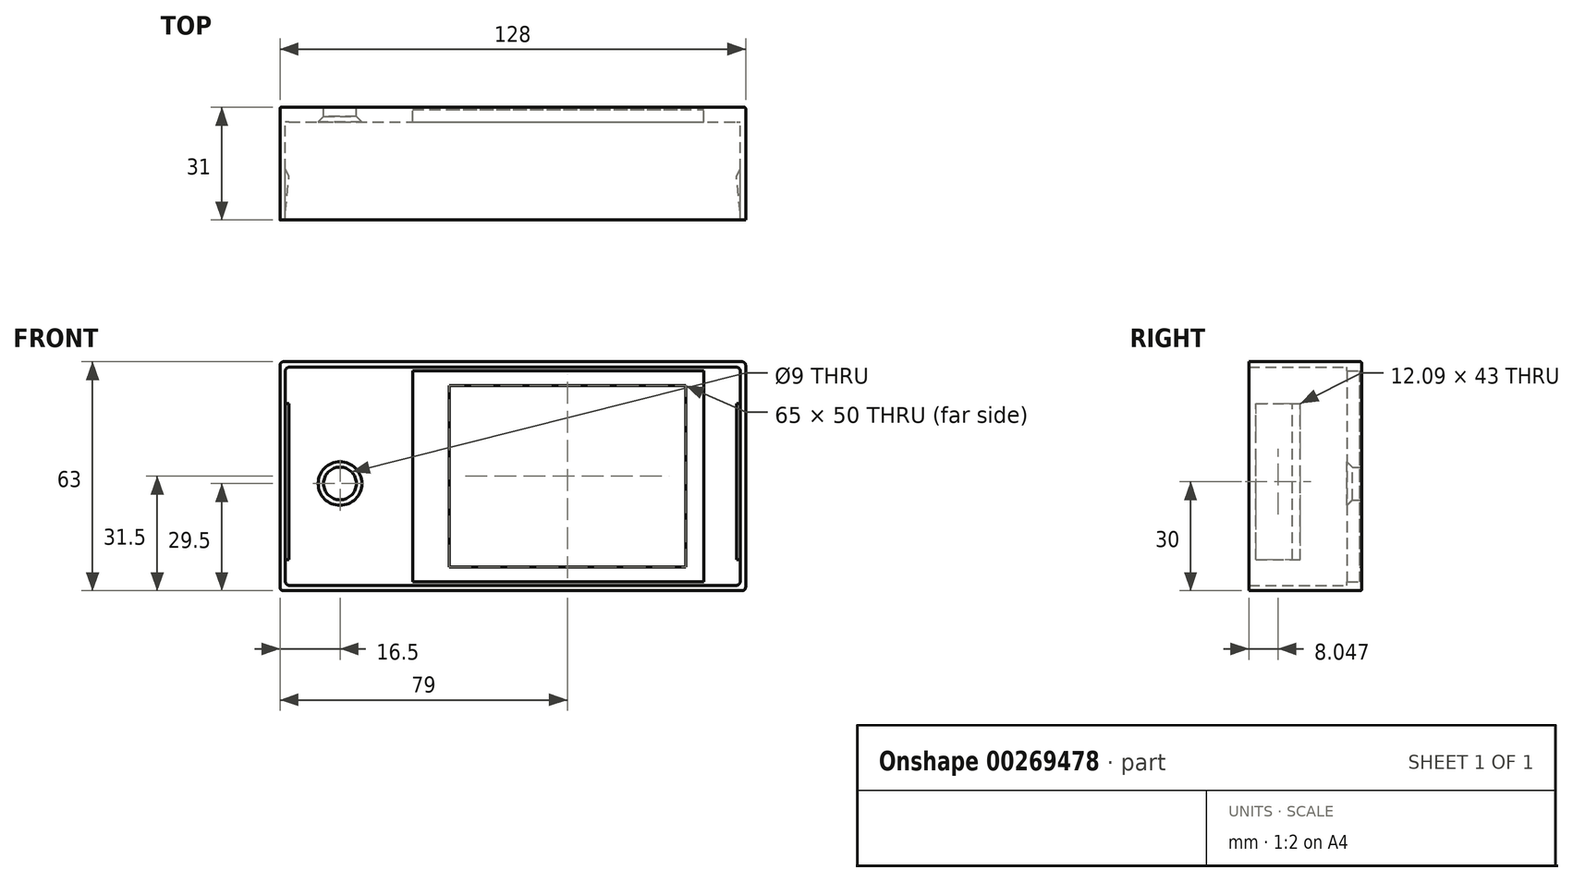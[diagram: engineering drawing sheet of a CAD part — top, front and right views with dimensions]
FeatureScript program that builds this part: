
annotation { "Feature Type Name" : "Feature", "Feature Type Description" : "" }
export const myFeature = defineFeature(function(context is Context, id is Id, definition is map)
    precondition{}
    {
        {
            var Q0;
            Q0=qCreatedBy(makeId("Front.planeOp"),FACE);
            var sketch = newSketch(context, id + "F0", { "sketchPlane" : qUnion([Q0])});
            skLineSegment(sketch, "E0.bottom", {"start": v(-64, 31.5) * mm, "end": v(64, 31.5) * mm});
            skLineSegment(sketch, "E0.top", {"start": v(-64, -31.5) * mm, "end": v(64, -31.5) * mm});
            skLineSegment(sketch, "E0.left", {"start": v(-64, 31.5) * mm, "end": v(-64, -31.5) * mm});
            skLineSegment(sketch, "E0.right", {"start": v(64, 31.5) * mm, "end": v(64, -31.5) * mm});
            skPoint(sketch, "E0.middle", {"position": v(0, 0) * mm});
            skLineSegment(sketch, "E1.0", {"start": v(-62.5, 30) * mm, "end": v(62.5, 30) * mm});
            skLineSegment(sketch, "E1.1", {"start": v(-62.5, 30) * mm, "end": v(-62.5, -30) * mm});
            skLineSegment(sketch, "E1.2", {"start": v(-62.5, -30) * mm, "end": v(62.5, -30) * mm});
            skLineSegment(sketch, "E1.3", {"start": v(62.5, 30) * mm, "end": v(62.5, -30) * mm});
            skLineSegment(sketch, "E2.bottom", {"start": v(-27.5, 29) * mm, "end": v(52.5, 29) * mm});
            skLineSegment(sketch, "E2.top", {"start": v(-27.5, -29) * mm, "end": v(52.5, -29) * mm});
            skLineSegment(sketch, "E2.left", {"start": v(-27.5, 29) * mm, "end": v(-27.5, -29) * mm});
            skLineSegment(sketch, "E2.right", {"start": v(52.5, 29) * mm, "end": v(52.5, -29) * mm});
            skLineSegment(sketch, "E3.bottom", {"start": v(-17.5, 25) * mm, "end": v(47.5, 25) * mm});
            skLineSegment(sketch, "E3.top", {"start": v(-17.5, -25) * mm, "end": v(47.5, -25) * mm});
            skLineSegment(sketch, "E3.left", {"start": v(-17.5, 25) * mm, "end": v(-17.5, -25) * mm});
            skLineSegment(sketch, "E3.right", {"start": v(47.5, 25) * mm, "end": v(47.5, -25) * mm});
            skCircle(sketch, "E4", {"center": v(-47.5, -2) * mm, "radius": 4.5 * mm});
            skSolve(sketch);
        }
        {
            var Q0;
            Q0=makeQuery(id+"F0.imprint","IMPRINT",FACE,{"disambiguationData":[TD([[makeQuery(id+"F0.imprint","IMPRINT",EDGE,{"derivedFrom":sQuery(id+"F0.wireOp",EDGE,"E0.bottom")}),-1.0]])]});
            extrude(context, id + "F1", {"entities" : qUnion([Q0]), "depth" : 31 * mm});
        }
        {
            var Q0;
            Q0=makeQuery(id+"F0.imprint","IMPRINT",FACE,{"disambiguationData":[TD([[makeQuery(id+"F0.imprint","IMPRINT",EDGE,{"derivedFrom":sQuery(id+"F0.wireOp",EDGE,"E2.bottom")}),-1.0]])]});
            var Q1;
            Q1=makeQuery(id+"F0.imprint","IMPRINT",FACE,{"disambiguationData":[TD([[makeQuery(id+"F0.imprint","IMPRINT",EDGE,{"derivedFrom":sQuery(id+"F0.wireOp",EDGE,"E1.0")}),-1.0]])]});
            extrude(context, id + "F2", {"entities" : qUnion([Q0, Q1]), "operationType" : NewBodyOperationType.ADD, "depth" : 4 * mm});
        }
        {
            var Q0;
            Q0=makeQuery(id+"F0.imprint","IMPRINT",FACE,{"disambiguationData":[TD([[makeQuery(id+"F0.imprint","IMPRINT",EDGE,{"derivedFrom":sQuery(id+"F0.wireOp",EDGE,"E2.bottom")}),-1.0]])]});
            extrude(context, id + "F3", {"entities" : qUnion([Q0]), "operationType" : NewBodyOperationType.REMOVE, "endBound" : BoundingType.UP_TO_NEXT, "depth" : 25 * mm, "hasSecondDirection" : true, "secondDirectionOppositeDirection" : false, "secondDirectionDepth" : 0.6 * mm});
        }
        {
            var Q0;
            Q0=makeQuery(id+"F1.opExtrude","CAP_EDGE",EDGE,{"disambiguationData":[OSD([sQuery(id+"F0.wireOp",EDGE,"E0.right")])],"isStart":true});
            var Q1;
            Q1=makeQuery(id+"F1.opExtrude","CAP_EDGE",EDGE,{"disambiguationData":[OSD([sQuery(id+"F0.wireOp",EDGE,"E0.bottom")])],"isStart":true});
            var Q2;
            Q2=makeQuery(id+"F1.opExtrude","CAP_EDGE",EDGE,{"disambiguationData":[OSD([sQuery(id+"F0.wireOp",EDGE,"E0.left")])],"isStart":true});
            var Q3;
            Q3=makeQuery(id+"F1.opExtrude","CAP_EDGE",EDGE,{"disambiguationData":[OSD([sQuery(id+"F0.wireOp",EDGE,"E0.top")])],"isStart":true});
            fillet(context, id + "F4", {"entities" : qUnion([Q0, Q1, Q2, Q3]), "radius" : 0.3 * mm, "tangentPropagation" : true, "allowEdgeOverflow" : false});
        }
        {
            var Q0;
            Q0=makeQuery(id+"F1.opExtrude","SWEPT_FACE",FACE,{"disambiguationData":[OSD([sQuery(id+"F0.wireOp",EDGE,"E1.0")])]});
            var sketch = newSketch(context, id + "F5", { "sketchPlane" : qUnion([Q0])});
            skLineSegment(sketch, "E5", {"start": v(-62.5, 29) * mm, "end": v(-61.5, 19.05) * mm});
            skLineSegment(sketch, "E6", {"start": v(-61.5, 19.05) * mm, "end": v(-62.5, 16.9) * mm});
            skLineSegment(sketch, "E7", {"start": v(-62.5, 16.9) * mm, "end": v(-62.5, 29) * mm});
            skLineSegment(sketch, "E8", {"start": v(62.5, 29) * mm, "end": v(61.5, 19.05) * mm});
            skLineSegment(sketch, "E9", {"start": v(61.5, 19.05) * mm, "end": v(62.5, 16.9) * mm});
            skLineSegment(sketch, "E10", {"start": v(62.5, 16.9) * mm, "end": v(62.5, 29) * mm});
            skSolve(sketch);
        }
        {
            var Q0;
            Q0 = qSketchRegion(id + "F5", true);
            extrude(context, id + "F6", {"entities" : qUnion([Q0]), "operationType" : NewBodyOperationType.ADD, "depth" : 53 * mm, "hasSecondDirection" : true, "secondDirectionOppositeDirection" : false, "secondDirectionDepth" : 10 * mm});
        }
        {
            var Q0;
            Q0=makeQuery(id+"F0.imprint","IMPRINT",FACE,{"disambiguationData":[TD([[makeQuery(id+"F0.imprint","IMPRINT",EDGE,{"derivedFrom":sQuery(id+"F0.wireOp",EDGE,"E1.0")}),-1.0]])]});
            var sketch = newSketch(context, id + "F7", { "sketchPlane" : qUnion([Q0])});
            skLineSegment(sketch, "E11.bottom", {"start": v(-27.5, 30) * mm, "end": v(-33.5, 30) * mm});
            skLineSegment(sketch, "E11.top", {"start": v(-27.5, -30) * mm, "end": v(-33.5, -30) * mm});
            skLineSegment(sketch, "E11.left", {"start": v(-27.5, 30) * mm, "end": v(-27.5, -30) * mm});
            skLineSegment(sketch, "E11.right", {"start": v(-33.5, 30) * mm, "end": v(-33.5, -30) * mm});
            skLineSegment(sketch, "E12.bottom", {"start": v(52.5, -30) * mm, "end": v(58.5, -30) * mm});
            skLineSegment(sketch, "E12.top", {"start": v(52.5, 30) * mm, "end": v(58.5, 30) * mm});
            skLineSegment(sketch, "E12.left", {"start": v(52.5, -30) * mm, "end": v(52.5, 30) * mm});
            skLineSegment(sketch, "E12.right", {"start": v(58.5, -30) * mm, "end": v(58.5, 30) * mm});
            skSolve(sketch);
        }
        {
            var Q0;
            Q0 = qSketchRegion(id + "F7", true);
            extrude(context, id + "F8", {"entities" : qUnion([Q0]), "operationType" : NewBodyOperationType.ADD, "depth" : 1 * mm});
        }
        {
            var Q0;
            Q0=makeQuery(id+"F1.opExtrude","SWEPT_EDGE",EDGE,{"disambiguationData":[OSD([sQuery(id+"F0.wireOp",EDGE,"E1.0"),sQuery(id+"F0.wireOp",EDGE,"E1.3")])]});
            var Q1;
            Q1=makeQuery(id+"F1.opExtrude","SWEPT_EDGE",EDGE,{"disambiguationData":[OSD([sQuery(id+"F0.wireOp",EDGE,"E1.0"),sQuery(id+"F0.wireOp",EDGE,"E1.1")])]});
            var Q2;
            Q2=makeQuery(id+"F1.opExtrude","SWEPT_EDGE",EDGE,{"disambiguationData":[OSD([sQuery(id+"F0.wireOp",EDGE,"E1.1"),sQuery(id+"F0.wireOp",EDGE,"E1.2")])]});
            var Q3;
            Q3=makeQuery(id+"F1.opExtrude","SWEPT_EDGE",EDGE,{"disambiguationData":[OSD([sQuery(id+"F0.wireOp",EDGE,"E1.2"),sQuery(id+"F0.wireOp",EDGE,"E1.3")])]});
            var Q4;
            Q4=makeQuery(id+"F1.opExtrude","SWEPT_EDGE",EDGE,{"disambiguationData":[OSD([sQuery(id+"F0.wireOp",EDGE,"E0.bottom"),sQuery(id+"F0.wireOp",EDGE,"E0.right")])]});
            var Q5;
            Q5=makeQuery(id+"F1.opExtrude","SWEPT_EDGE",EDGE,{"disambiguationData":[OSD([sQuery(id+"F0.wireOp",EDGE,"E0.top"),sQuery(id+"F0.wireOp",EDGE,"E0.right")])]});
            var Q6;
            Q6=makeQuery(id+"F1.opExtrude","SWEPT_EDGE",EDGE,{"disambiguationData":[OSD([sQuery(id+"F0.wireOp",EDGE,"E0.bottom"),sQuery(id+"F0.wireOp",EDGE,"E0.left")])]});
            var Q7;
            Q7=makeQuery(id+"F1.opExtrude","SWEPT_EDGE",EDGE,{"disambiguationData":[OSD([sQuery(id+"F0.wireOp",EDGE,"E0.top"),sQuery(id+"F0.wireOp",EDGE,"E0.left")])]});
            fillet(context, id + "F9", {"entities" : qUnion([Q0, Q1, Q2, Q3, Q4, Q5, Q6, Q7]), "radius" : 1 * mm, "tangentPropagation" : true, "allowEdgeOverflow" : false});
        }
        {
            var Q0;
            Q0=makeQuery(id+"F2.opExtrude","CAP_EDGE",EDGE,{"disambiguationData":[OSD([sQuery(id+"F0.wireOp",EDGE,"E4")])],"isStart":false});
            chamfer(context, id + "F10", {"entities" : qUnion([Q0]), "width" : 1.5 * mm, "tangentPropagation" : true});
        }
    });
